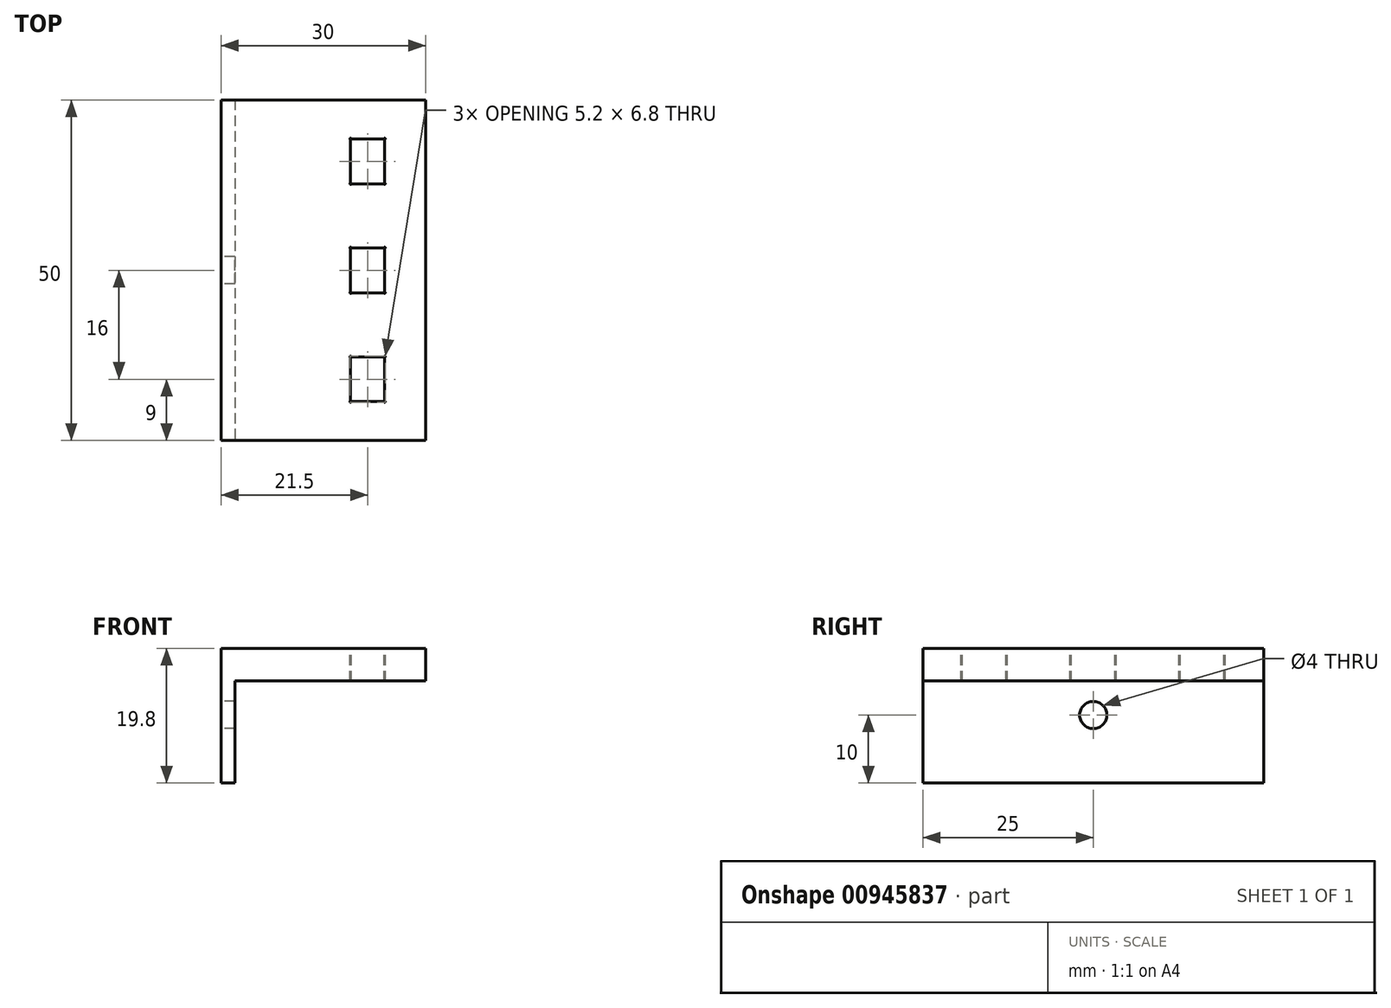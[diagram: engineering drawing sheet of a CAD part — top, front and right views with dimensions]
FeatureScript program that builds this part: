
annotation { "Feature Type Name" : "Feature", "Feature Type Description" : "" }
export const myFeature = defineFeature(function(context is Context, id is Id, definition is map)
    precondition{}
    {
        {
            assignVariable(context, id + "F0", {"name" : "width", "anyValue" : 50});
        }
        {
            var Q0;
            Q0=qCreatedBy(makeId("Front.planeOp"),FACE);
            var sketch = newSketch(context, id + "F1", { "sketchPlane" : qUnion([Q0])});
            skLineSegment(sketch, "E0", {"start": v(0, 0) * mm, "end": v(0, 19.8) * mm});
            skLineSegment(sketch, "E1", {"start": v(0, 19.8) * mm, "end": v(30, 19.8) * mm});
            skLineSegment(sketch, "E2", {"start": v(30, 19.8) * mm, "end": v(30, 15) * mm});
            skLineSegment(sketch, "E3", {"start": v(30, 15) * mm, "end": v(2, 15) * mm});
            skLineSegment(sketch, "E4", {"start": v(2, 15) * mm, "end": v(2, 0) * mm});
            skLineSegment(sketch, "E5", {"start": v(2, 0) * mm, "end": v(0, 0) * mm});
            skSolve(sketch);
        }
        {
            var Q0;
            Q0 = qSketchRegion(id + "F1", true);
            extrude(context, id + "F2", {"entities" : qUnion([Q0]), "oppositeDirection" : true, "depth" : (getVariable(context, 'width')) * mm, "offsetDistance" : 25 * mm});
        }
        {
            var Q0;
            Q0=makeQuery(id+"F2.opExtrude","SWEPT_FACE",FACE,{"disambiguationData":[OSD([sQuery(id+"F1.wireOp",EDGE,"E1")])]});
            var sketch = newSketch(context, id + "F3", { "sketchPlane" : qUnion([Q0])});
            skLineSegment(sketch, "E6", {"start": v(0, 25) * mm, "end": v(24, 25) * mm, "construction": true});
            skLineSegment(sketch, "E7", {"start": v(24, 21.7) * mm, "end": v(24, 25) * mm, "construction": true});
            skLineSegment(sketch, "E8.bottom", {"start": v(24, 21.7) * mm, "end": v(19, 21.7) * mm});
            skLineSegment(sketch, "E8.top", {"start": v(24, 28.3) * mm, "end": v(19, 28.3) * mm});
            skLineSegment(sketch, "E8.left", {"start": v(24, 21.7) * mm, "end": v(24, 28.3) * mm});
            skLineSegment(sketch, "E8.right", {"start": v(19, 21.7) * mm, "end": v(19, 28.3) * mm});
            skCircle(sketch, "E9", {"center": v(19, 21.7) * mm, "radius": 0.1 * mm});
            skCircle(sketch, "E10", {"center": v(24, 21.7) * mm, "radius": 0.1 * mm});
            skCircle(sketch, "E11", {"center": v(24, 28.3) * mm, "radius": 0.1 * mm});
            skCircle(sketch, "E12", {"center": v(19, 28.3) * mm, "radius": 0.1 * mm});
            skPoint(sketch, "E13", {"position": v(24, 25) * mm});
            skLineSegment(sketch, "E14.direction1", {"start": v(24, 21.7) * mm, "end": v(49, 21.7) * mm, "construction": true});
            skLineSegment(sketch, "E15", {"start": v(6.36, 33) * mm, "end": v(22.45, 33) * mm});
            skLineSegment(sketch, "E16.MirrorCS", {"start": v(24, 37.7) * mm, "end": v(19, 37.7) * mm});
            skCircle(sketch, "E17.MirrorC", {"center": v(19, 37.7) * mm, "radius": 0.1 * mm});
            skLineSegment(sketch, "E18.MirrorCS", {"start": v(19, 44.3) * mm, "end": v(19, 37.7) * mm});
            skCircle(sketch, "E19.MirrorC", {"center": v(19, 44.3) * mm, "radius": 0.1 * mm});
            skLineSegment(sketch, "E20.MirrorCS", {"start": v(24, 44.3) * mm, "end": v(19, 44.3) * mm});
            skCircle(sketch, "E21.MirrorC", {"center": v(24, 44.3) * mm, "radius": 0.1 * mm});
            skLineSegment(sketch, "E22.MirrorCS", {"start": v(24, 44.3) * mm, "end": v(24, 41) * mm, "construction": true});
            skLineSegment(sketch, "E23.MirrorCS", {"start": v(24, 44.3) * mm, "end": v(24, 37.7) * mm});
            skCircle(sketch, "E24.MirrorC", {"center": v(24, 37.7) * mm, "radius": 0.1 * mm});
            skLineSegment(sketch, "E25", {"start": v(17, 17) * mm, "end": v(3.76, 17) * mm});
            skLineSegment(sketch, "E26.MirrorCS", {"start": v(24, 12.3) * mm, "end": v(19, 12.3) * mm});
            skCircle(sketch, "E27.MirrorC", {"center": v(19, 12.3) * mm, "radius": 0.1 * mm});
            skLineSegment(sketch, "E28.MirrorCS", {"start": v(19, 12.3) * mm, "end": v(19, 5.7) * mm});
            skCircle(sketch, "E29.MirrorC", {"center": v(19, 5.7) * mm, "radius": 0.1 * mm});
            skLineSegment(sketch, "E30.MirrorCS", {"start": v(24, 5.7) * mm, "end": v(19, 5.7) * mm});
            skCircle(sketch, "E31.MirrorC", {"center": v(24, 5.7) * mm, "radius": 0.1 * mm});
            skLineSegment(sketch, "E32.MirrorCS", {"start": v(24, 12.3) * mm, "end": v(24, 5.7) * mm});
            skCircle(sketch, "E33.MirrorC", {"center": v(24, 12.3) * mm, "radius": 0.1 * mm});
            skSolve(sketch);
        }
        {
            var Q0;
            Q0=makeQuery(id+"F2.opExtrude","SWEPT_FACE",FACE,{"disambiguationData":[OSD([sQuery(id+"F1.wireOp",EDGE,"E0")])]});
            var sketch = newSketch(context, id + "F4", { "sketchPlane" : qUnion([Q0])});
            skLineSegment(sketch, "E34", {"start": v(-25, 0) * mm, "end": v(-25, 10) * mm, "construction": true});
            skCircle(sketch, "E35", {"center": v(-25, 10) * mm, "radius": 2 * mm});
            skSolve(sketch);
        }
        {
            var Q0;
            Q0 = qSketchRegion(id + "F4", true);
            var Q1;
            Q1=makeQuery(id+"F2.opExtrude","SWEPT_FACE",FACE,{"disambiguationData":[OSD([sQuery(id+"F1.wireOp",EDGE,"E4")])]});
            extrude(context, id + "F5", {"entities" : qUnion([Q0]), "operationType" : NewBodyOperationType.REMOVE, "endBound" : BoundingType.UP_TO_SURFACE, "oppositeDirection" : true, "depth" : 25 * mm, "endBoundEntityFace" : qUnion([Q1]), "offsetDistance" : 25 * mm});
        }
        {
            var Q0;
            Q0 = qSketchRegion(id + "F3", true);
            extrude(context, id + "F6", {"entities" : qUnion([Q0]), "operationType" : NewBodyOperationType.REMOVE, "endBound" : BoundingType.UP_TO_NEXT, "oppositeDirection" : true, "depth" : 25 * mm, "offsetDistance" : 25 * mm});
        }
    });
